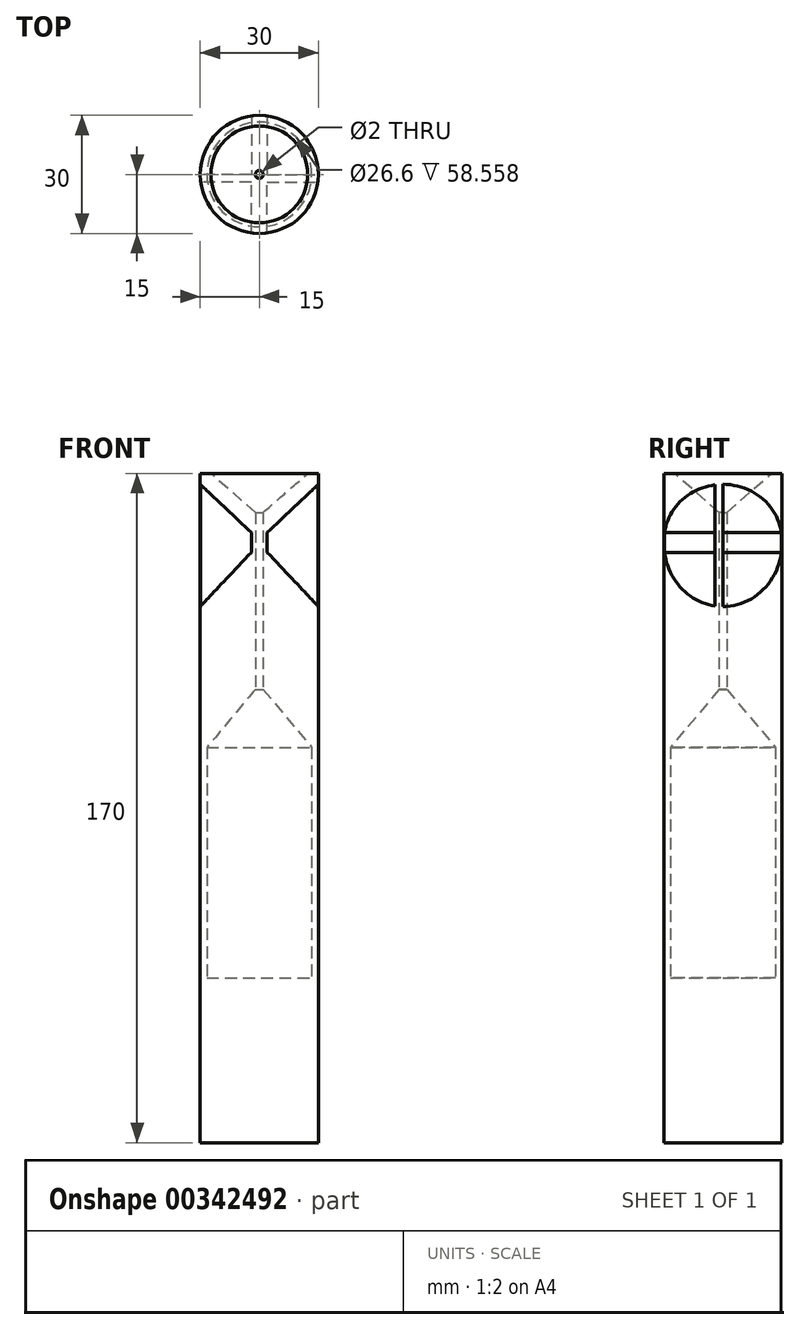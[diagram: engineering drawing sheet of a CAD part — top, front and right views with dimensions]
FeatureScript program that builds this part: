
annotation { "Feature Type Name" : "Feature", "Feature Type Description" : "" }
export const myFeature = defineFeature(function(context is Context, id is Id, definition is map)
    precondition{}
    {
        {
            var Q0;
            Q0=qCreatedBy(makeId("Top.planeOp"),FACE);
            var sketch = newSketch(context, id + "F0", { "sketchPlane" : qUnion([Q0])});
            skCircle(sketch, "E0", {"center": v(0, 0) * mm, "radius": 15 * mm});
            skSolve(sketch);
        }
        {
            var Q0;
            Q0=makeQuery(id+"F0.imprint","IMPRINT",FACE,{"disambiguationData":[TD([[makeQuery(id+"F0.imprint","IMPRINT",EDGE,{"derivedFrom":sQuery(id+"F0.wireOp",EDGE,"E0")}),1.0]])]});
            extrude(context, id + "F1", {"entities" : qUnion([Q0]), "depth" : 120 * mm, "hasSecondDirection" : true, "secondDirectionOppositeDirection" : true, "secondDirectionDepth" : 50 * mm, "offsetDistance" : 25 * mm});
        }
        {
            var Q0;
            Q0=qCreatedBy(makeId("Front.planeOp"),FACE);
            var sketch = newSketch(context, id + "F2", { "sketchPlane" : qUnion([Q0])});
            skLineSegment(sketch, "E1.left", {"start": v(-17, 105) * mm, "end": v(-17, 70) * mm});
            skLineSegment(sketch, "E1.right", {"start": v(-2, 105) * mm, "end": v(-2, 100) * mm});
            skLineSegment(sketch, "E2", {"start": v(-2, 105) * mm, "end": v(-17.89, 120) * mm});
            skLineSegment(sketch, "E3", {"start": v(-17.89, 120) * mm, "end": v(-17, 105) * mm});
            skLineSegment(sketch, "E4", {"start": v(-2, 100) * mm, "end": v(-17.89, 83.18) * mm});
            skLineSegment(sketch, "E5", {"start": v(-17.89, 83.18) * mm, "end": v(-17, 70) * mm});
            skLineSegment(sketch, "E6.MirrorCS", {"start": v(17.89, 83.18) * mm, "end": v(17, 70) * mm});
            skLineSegment(sketch, "E7.MirrorCS", {"start": v(2, 100) * mm, "end": v(17.89, 83.18) * mm});
            skLineSegment(sketch, "E8.MirrorCS", {"start": v(17.89, 120) * mm, "end": v(17, 105) * mm});
            skLineSegment(sketch, "E9.MirrorCS", {"start": v(2, 105) * mm, "end": v(17.89, 120) * mm});
            skLineSegment(sketch, "E10.MirrorCS", {"start": v(17, 105) * mm, "end": v(17, 70) * mm});
            skLineSegment(sketch, "E11.MirrorCS", {"start": v(2, 105) * mm, "end": v(2, 100) * mm});
            skSolve(sketch);
        }
        {
            var Q0;
            Q0 = qSketchRegion(id + "F2", true);
            extrude(context, id + "F3", {"entities" : qUnion([Q0]), "operationType" : NewBodyOperationType.REMOVE, "depth" : 25 * mm, "hasSecondDirection" : true, "secondDirectionOppositeDirection" : false, "secondDirectionDepth" : 2 * mm});
        }
        {
            var Q0;
            Q0 = qSketchRegion(id + "F2", true);
            extrude(context, id + "F4", {"entities" : qUnion([Q0]), "operationType" : NewBodyOperationType.REMOVE, "oppositeDirection" : true, "depth" : 25 * mm});
        }
        {
            var Q0;
            Q0=qCreatedBy(makeId("Front.planeOp"),FACE);
            var sketch = newSketch(context, id + "F5", { "sketchPlane" : qUnion([Q0])});
            skLineSegment(sketch, "E12", {"start": v(-15.87, 123.12) * mm, "end": v(0, 123.12) * mm});
            skLineSegment(sketch, "E13", {"start": v(0, 123.12) * mm, "end": v(0, 110.12) * mm});
            skLineSegment(sketch, "E14.left", {"start": v(0, 110.12) * mm, "end": v(0, 65.12) * mm});
            skLineSegment(sketch, "E14.right", {"start": v(-1, 110.12) * mm, "end": v(-1, 65.12) * mm});
            skLineSegment(sketch, "E15", {"start": v(-1, 110.12) * mm, "end": v(-15.87, 123.12) * mm});
            skLineSegment(sketch, "E16", {"start": v(-1, 65.12) * mm, "end": v(-13.3, 50.46) * mm});
            skLineSegment(sketch, "E17", {"start": v(-13.3, 50.46) * mm, "end": v(-13.3, -8.1) * mm});
            skLineSegment(sketch, "E18", {"start": v(-13.3, -8.1) * mm, "end": v(0, -8.1) * mm});
            skLineSegment(sketch, "E19", {"start": v(0, -8.1) * mm, "end": v(0, 65.12) * mm});
            skSolve(sketch);
        }
        {
            var Q0;
            Q0 = qSketchRegion(id + "F5", true);
            var Q1;
            Q1=sQuery(id+"F5.wireOp",EDGE,"E13");
            revolve(context, id + "F6", {"operationType" : NewBodyOperationType.REMOVE, "entities" : qUnion([Q0]), "axis" : qUnion([Q1]), "revolveType" : RevolveType.FULL, "oppositeDirection" : true});
        }
    });
